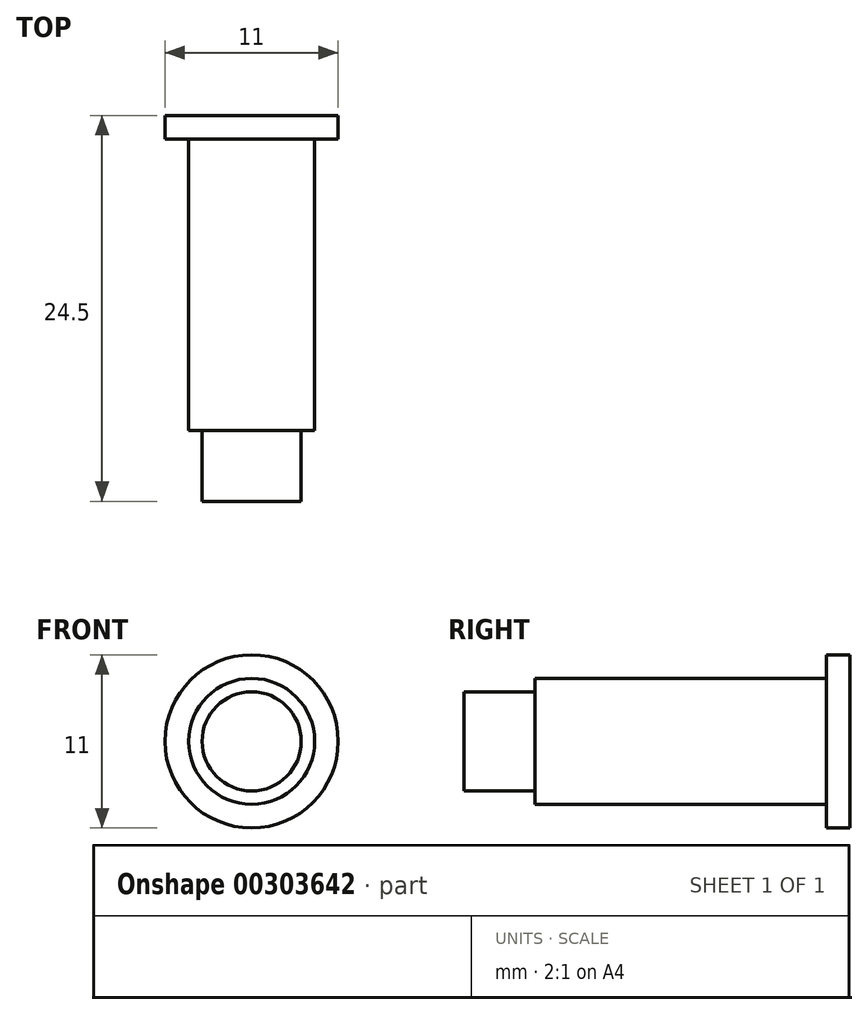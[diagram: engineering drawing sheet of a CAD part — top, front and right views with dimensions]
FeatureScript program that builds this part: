
annotation { "Feature Type Name" : "Feature", "Feature Type Description" : "" }
export const myFeature = defineFeature(function(context is Context, id is Id, definition is map)
    precondition{}
    {
        {
            var Q0;
            Q0=qCreatedBy(makeId("Front.planeOp"),FACE);
            var sketch = newSketch(context, id + "F0", { "sketchPlane" : qUnion([Q0])});
            skCircle(sketch, "E0", {"center": v(0, 0) * mm, "radius": 5.5 * mm});
            skCircle(sketch, "E1", {"center": v(0, 0) * mm, "radius": 4 * mm});
            skCircle(sketch, "E2", {"center": v(0, 0) * mm, "radius": 3.15 * mm});
            skSolve(sketch);
        }
        {
            var Q0;
            Q0=makeQuery(id+"F0.imprint","IMPRINT",FACE,{"disambiguationData":[TD([[makeQuery(id+"F0.imprint","IMPRINT",EDGE,{"derivedFrom":sQuery(id+"F0.wireOp",EDGE,"E2")}),1.0]])]});
            extrude(context, id + "F1", {"entities" : qUnion([Q0]), "depth" : 24.5 * mm});
        }
        {
            var Q0;
            Q0=makeQuery(id+"F0.imprint","IMPRINT",FACE,{"disambiguationData":[TD([[makeQuery(id+"F0.imprint","IMPRINT",EDGE,{"derivedFrom":sQuery(id+"F0.wireOp",EDGE,"E1")}),1.0]])]});
            extrude(context, id + "F2", {"entities" : qUnion([Q0]), "operationType" : NewBodyOperationType.ADD, "depth" : 20 * mm});
        }
        {
            var Q0;
            Q0=makeQuery(id+"F0.imprint","IMPRINT",FACE,{"disambiguationData":[TD([[makeQuery(id+"F0.imprint","IMPRINT",EDGE,{"derivedFrom":sQuery(id+"F0.wireOp",EDGE,"E0")}),1.0]])]});
            extrude(context, id + "F3", {"entities" : qUnion([Q0]), "operationType" : NewBodyOperationType.ADD, "depth" : 1.5 * mm});
        }
    });
